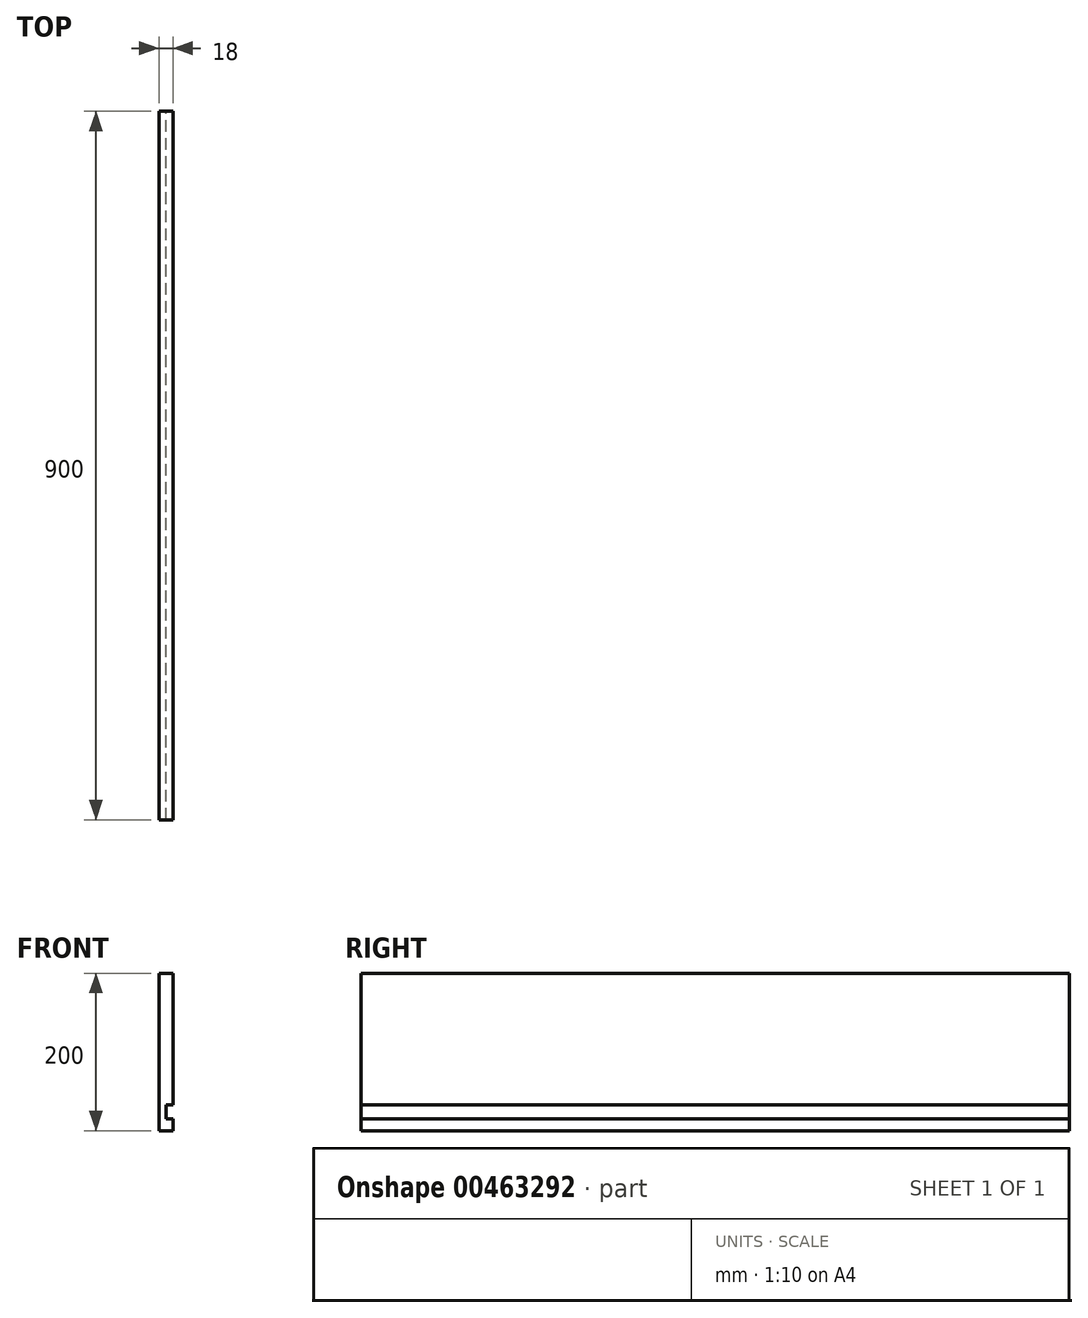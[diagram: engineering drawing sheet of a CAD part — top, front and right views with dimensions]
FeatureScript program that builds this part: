
annotation { "Feature Type Name" : "Feature", "Feature Type Description" : "" }
export const myFeature = defineFeature(function(context is Context, id is Id, definition is map)
    precondition{}
    {
        {
            var Q0;
            Q0=qCreatedBy(makeId("Right.planeOp"),FACE);
            var sketch = newSketch(context, id + "F0", { "sketchPlane" : qUnion([Q0])});
            skLineSegment(sketch, "E0.bottom", {"start": v(0, 0) * mm, "end": v(900, 0) * mm});
            skLineSegment(sketch, "E0.top", {"start": v(0, -200) * mm, "end": v(900, -200) * mm});
            skLineSegment(sketch, "E0.left", {"start": v(0, 0) * mm, "end": v(0, -200) * mm});
            skLineSegment(sketch, "E0.right", {"start": v(900, 0) * mm, "end": v(900, -200) * mm});
            skSolve(sketch);
        }
        {
            var Q0;
            Q0 = qSketchRegion(id + "F0", true);
            extrude(context, id + "F1", {"entities" : qUnion([Q0]), "depth" : 18 * mm});
        }
        {
            var Q0;
            Q0=makeQuery(id+"F1.opExtrude","CAP_FACE",FACE,{"disambiguationData":[OSD([sQuery(id+"F0.wireOp",EDGE,"E0.bottom"),sQuery(id+"F0.wireOp",EDGE,"E0.top"),sQuery(id+"F0.wireOp",EDGE,"E0.left"),sQuery(id+"F0.wireOp",EDGE,"E0.right")])],"isStart":false});
            var sketch = newSketch(context, id + "F2", { "sketchPlane" : qUnion([Q0])});
            skLineSegment(sketch, "E1.bottom", {"start": v(0, -167) * mm, "end": v(900, -167) * mm});
            skLineSegment(sketch, "E1.top", {"start": v(0, -185) * mm, "end": v(900, -185) * mm});
            skLineSegment(sketch, "E1.left", {"start": v(0, -167) * mm, "end": v(0, -185) * mm});
            skLineSegment(sketch, "E1.right", {"start": v(900, -167) * mm, "end": v(900, -185) * mm});
            skSolve(sketch);
        }
        {
            var Q0;
            Q0=makeQuery(id+"F2.imprint","IMPRINT",FACE,{"disambiguationData":[TD([[makeQuery(id+"F2.imprint","IMPRINT",EDGE,{"derivedFrom":sQuery(id+"F2.wireOp",EDGE,"E1.bottom")}),-1.0]])]});
            extrude(context, id + "F3", {"entities" : qUnion([Q0]), "operationType" : NewBodyOperationType.REMOVE, "oppositeDirection" : true, "depth" : 9 * mm});
        }
    });
